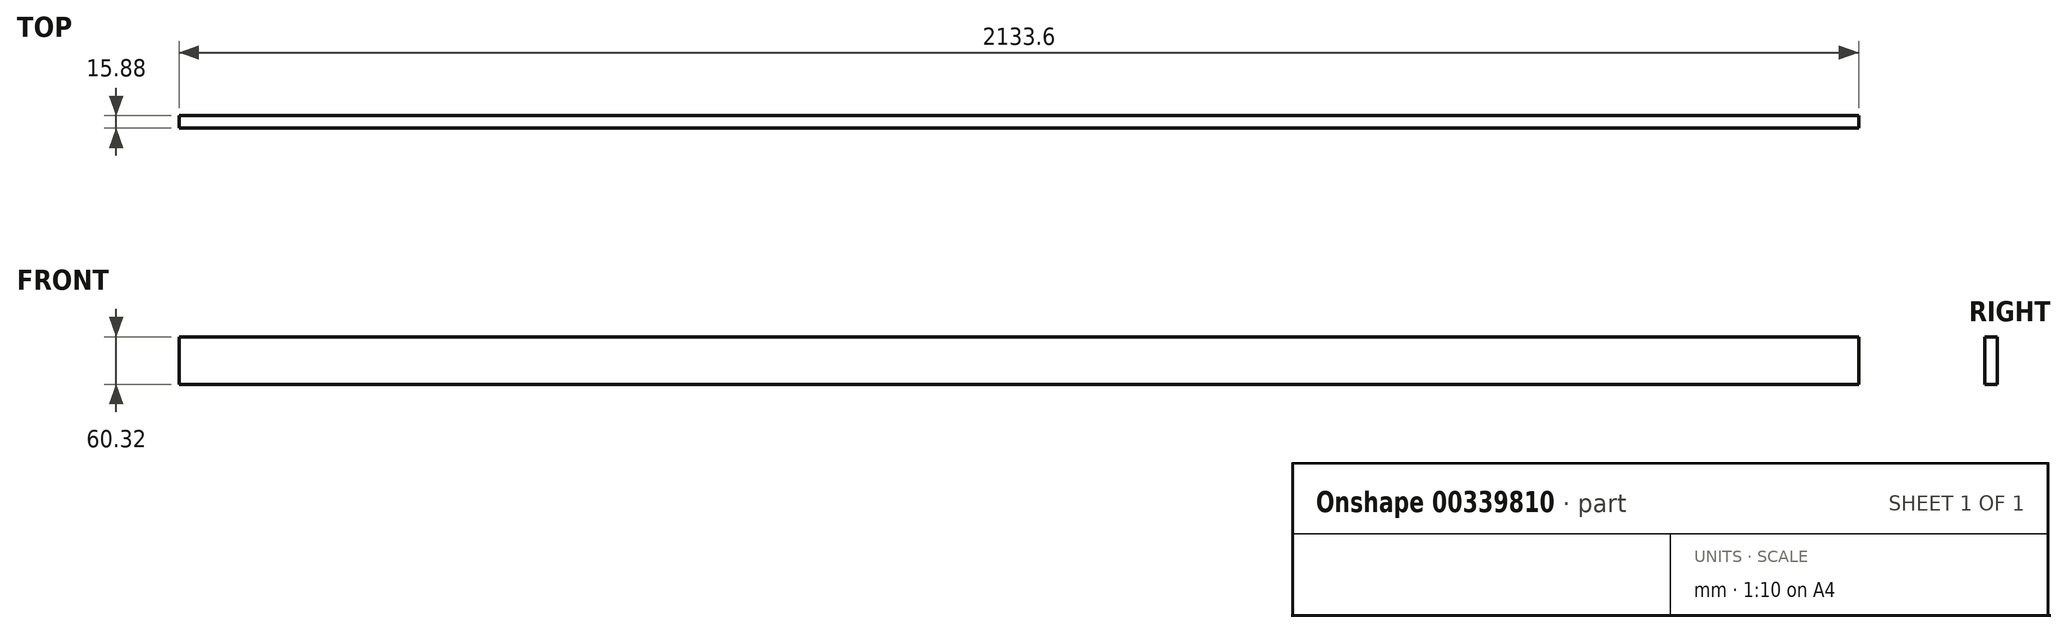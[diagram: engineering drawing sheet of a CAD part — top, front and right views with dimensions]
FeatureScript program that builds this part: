
annotation { "Feature Type Name" : "Feature", "Feature Type Description" : "" }
export const myFeature = defineFeature(function(context is Context, id is Id, definition is map)
    precondition{}
    {
        {
            var Q0;
            Q0=qCreatedBy(makeId("Front.planeOp"),FACE);
            var sketch = newSketch(context, id + "F0", { "sketchPlane" : qUnion([Q0])});
            skLineSegment(sketch, "E0.bottom", {"start": v(-127.2, 40.41) * mm, "end": v(2006.4, 40.41) * mm});
            skLineSegment(sketch, "E0.top", {"start": v(-127.2, -19.91) * mm, "end": v(2006.4, -19.91) * mm});
            skLineSegment(sketch, "E0.left", {"start": v(-127.2, 40.41) * mm, "end": v(-127.2, -19.91) * mm});
            skLineSegment(sketch, "E0.right", {"start": v(2006.4, 40.41) * mm, "end": v(2006.4, -19.91) * mm});
            skSolve(sketch);
        }
        {
            var Q0;
            Q0 = qSketchRegion(id + "F0", true);
            extrude(context, id + "F1", {"entities" : qUnion([Q0]), "oppositeDirection" : true, "depth" : 15.88 * mm});
        }
    });
